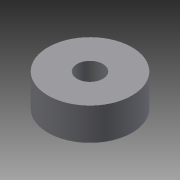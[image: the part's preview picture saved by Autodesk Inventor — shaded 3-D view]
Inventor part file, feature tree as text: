
AUTODESK INVENTOR PART (.ipt)
format: ipt  version: 2013 SP2 (Build 170200200, 200)  size: 73,728 bytes
history: native  units: mm
features: extrude x1, sketch x1
ambient origin geometry x8: Origin, YZ Plane, XZ Plane, XY Plane, X Axis, Y Axis, Z Axis, Center Point
bodies: Solid1 (feature_tree)
feature tree (2):
  extrude  "Extrusion1"  Depth=4.0mm
  sketch  "Sketch1"  dims[d0=13.0mm d2=4.0mm d3=5.0mm d4=0.0mm]
